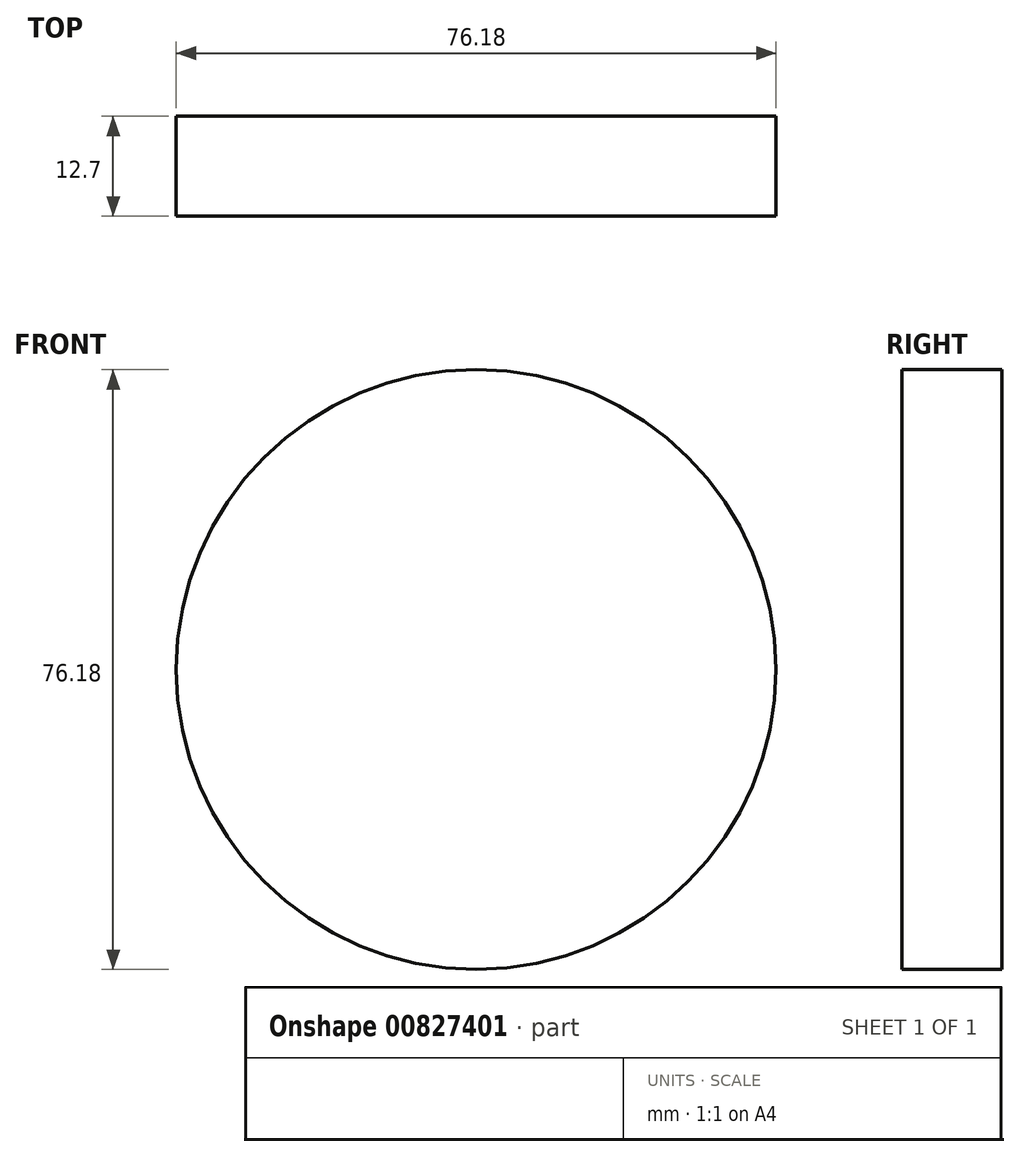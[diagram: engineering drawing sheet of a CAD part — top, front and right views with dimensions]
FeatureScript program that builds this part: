
annotation { "Feature Type Name" : "Feature", "Feature Type Description" : "" }
export const myFeature = defineFeature(function(context is Context, id is Id, definition is map)
    precondition{}
    {
        {
            var Q0;
            Q0=qCreatedBy(makeId("Front.planeOp"),FACE);
            var sketch = newSketch(context, id + "F0", { "sketchPlane" : qUnion([Q0])});
            skCircle(sketch, "E0", {"center": v(0, 2.14) * mm, "radius": 38.1 * mm});
            skSolve(sketch);
        }
        {
            var Q0;
            Q0 = qSketchRegion(id + "F0", true);
            extrude(context, id + "F1", {"entities" : qUnion([Q0]), "endBound" : BoundingType.SYMMETRIC, "depth" : 12.7 * mm, "offsetDistance" : 25.4 * mm});
        }
    });
